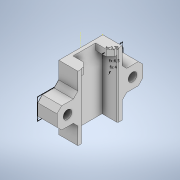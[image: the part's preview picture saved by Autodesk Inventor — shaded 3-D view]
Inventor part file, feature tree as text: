
AUTODESK INVENTOR PART (.ipt)
format: ipt  version: 2021 (Build 250183000, 183)  size: 444,928 bytes
history: native  units: mm
features: chamfer x5, extrude x4, sketch x4, other x1, projected_geometry x1
ambient origin geometry x8: Origin, YZ Plane, XZ Plane, XY Plane, X Axis, Y Axis, Z Axis, Center Point
bodies: Solid1 (feature_tree)
feature tree (15):
  extrude  "Extrusion1"  Depth=16.5mm
  sketch  "Sketch2"  dims[d6=2.0mm d7=2.0mm]
  other  "Work Point1"
  sketch  "Sketch3"  dims[d8=30.0mm d9=0.0mm]
  extrude  "Extrusion2"  Depth=2.0mm
  extrude  "Extrusion3"  TaperAngle=0.0deg  [1 undecoded]
  chamfer  "Chamfer1"  Distance=4.0mm
  chamfer  "Chamfer2"  Distance=20.0mm
  chamfer  "Chamfer3"  Distance=6.5mm
  chamfer  "Chamfer4"  Distance=3.65mm
  extrude  "Extrusion4"  TaperAngle=0.0deg  [1 undecoded]
  chamfer  "Chamfer5"  Distance=2.0mm Angle=45.0deg
  sketch  "Sketch1"  dims[d4=7.3mm d5=16.5mm]
  sketch  "Sketch4"  dims[d10=9.75mm d11=4.0mm d12=20.0mm d13=0.0mm d14=6.5mm d15=3.65mm d16=0.0mm d17=2.166667mm d18=2.0mm d19=45.0deg d20=0.4mm d21=2.0mm d22=45.0deg d23=0.4mm d24=2.0mm d25=45.0deg d26=1.25mm d27=2.0mm d28=45.0deg d29=3.0mm d30=3.0mm d31=3.0mm d32=0.0mm d33=2.0mm d34=2.0mm d35=45.0deg]
  projected_geometry  "Projected Loop1"
note: 2 required parameter values undecoded (feature->parameter linkage not recoverable at this tier; creation-order binding heuristic only, values carry confidence <= 0.55)
